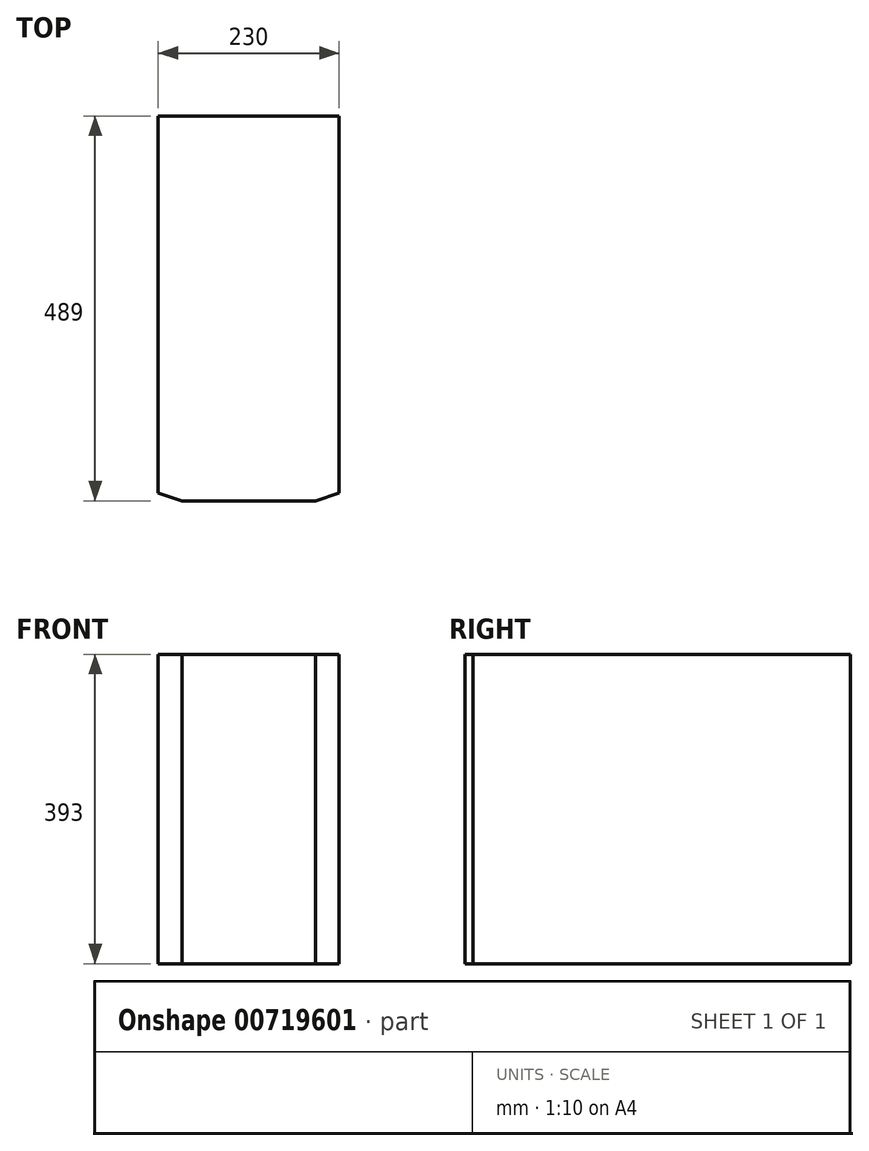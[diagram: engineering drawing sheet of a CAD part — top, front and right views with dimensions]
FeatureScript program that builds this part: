
annotation { "Feature Type Name" : "Feature", "Feature Type Description" : "" }
export const myFeature = defineFeature(function(context is Context, id is Id, definition is map)
    precondition{}
    {
        {
            var Q0;
            Q0=qCreatedBy(makeId("Front.planeOp"),FACE);
            var sketch = newSketch(context, id + "F0", { "sketchPlane" : qUnion([Q0])});
            skLineSegment(sketch, "E0.bottom", {"start": v(0, 0) * mm, "end": v(230, 0) * mm});
            skLineSegment(sketch, "E0.top", {"start": v(0, 393) * mm, "end": v(230, 393) * mm});
            skLineSegment(sketch, "E0.left", {"start": v(0, 0) * mm, "end": v(0, 393) * mm});
            skLineSegment(sketch, "E0.right", {"start": v(230, 0) * mm, "end": v(230, 393) * mm});
            skSolve(sketch);
        }
        {
            var Q0;
            Q0 = qSketchRegion(id + "F0", true);
            extrude(context, id + "F1", {"entities" : qUnion([Q0]), "oppositeDirection" : true, "depth" : 489 * mm, "offsetDistance" : 25 * mm});
        }
        {
            var Q0;
            Q0=makeQuery(id+"F1.opExtrude","CAP_EDGE",EDGE,{"disambiguationData":[OSD([sQuery(id+"F0.wireOp",EDGE,"E0.right")])],"isStart":true});
            var Q1;
            Q1=makeQuery(id+"F1.opExtrude","CAP_EDGE",EDGE,{"disambiguationData":[OSD([sQuery(id+"F0.wireOp",EDGE,"E0.left")])],"isStart":true});
            chamfer(context, id + "F2", {"entities" : qUnion([Q0, Q1]), "chamferType" : ChamferType.TWO_OFFSETS, "width1" : 30 * mm, "oppositeDirection" : false, "width2" : 10 * mm, "tangentPropagation" : true});
        }
    });
